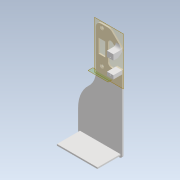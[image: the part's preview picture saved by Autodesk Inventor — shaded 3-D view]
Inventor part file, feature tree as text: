
AUTODESK INVENTOR PART (.ipt)
format: ipt  version: 2020.2 (Build 242310000, 310)  size: 3,894,272 bytes
history: native  units: in
note: dims shown in document units (in); Inventor stores cm internally (conversion verified against a paired STEP export)
features: extrude x4, sketch x4, other x2, plane x2, fillet x2, split x1, thicken_offset x1
ambient origin geometry x8: Origin, YZ Plane, XZ Plane, XY Plane, X Axis, Y Axis, Z Axis, Center Point
bodies: Solid1 (feature_tree)
feature tree (16):
  other  "ble_switch_mount"
  plane  "Work Plane1"
  other  "MeshFeature1"
  split  "Split1"
  extrude  "Extrusion1"  Depth=0.3937in TaperAngle=0.0deg
  extrude  "Extrusion3"  Depth=0.002in
  plane  "Work Plane2"
  extrude  "Extrusion4"  Depth=0.6299in TaperAngle=0.0deg
  thicken_offset  "Thicken1"
  fillet  "Fillet2"  Radius=4.5276in
  fillet  "Fillet3"  Radius=3.1496in
  extrude  "Extrusion5"  Depth=1.6437in
  sketch  "Sketch2"  dims[d1=0.002in d3=0.3937in d4=0.0in]
  sketch  "Sketch3"  dims[d5=0.002in d6=0.002in]
  sketch  "Sketch4"  dims[d7=0.002in d10=0.6299in d11=0.0in d12=4.5276in d13=3.1496in]
  sketch  "Sketch5"  dims[d15=0.3937in d16=0.0in d17=0.2953in d18=0.2953in d19=1.5748in d26=1.5748in d27=2.3622in d28=0.1969in d29=1.6437in d30=0.0in]
